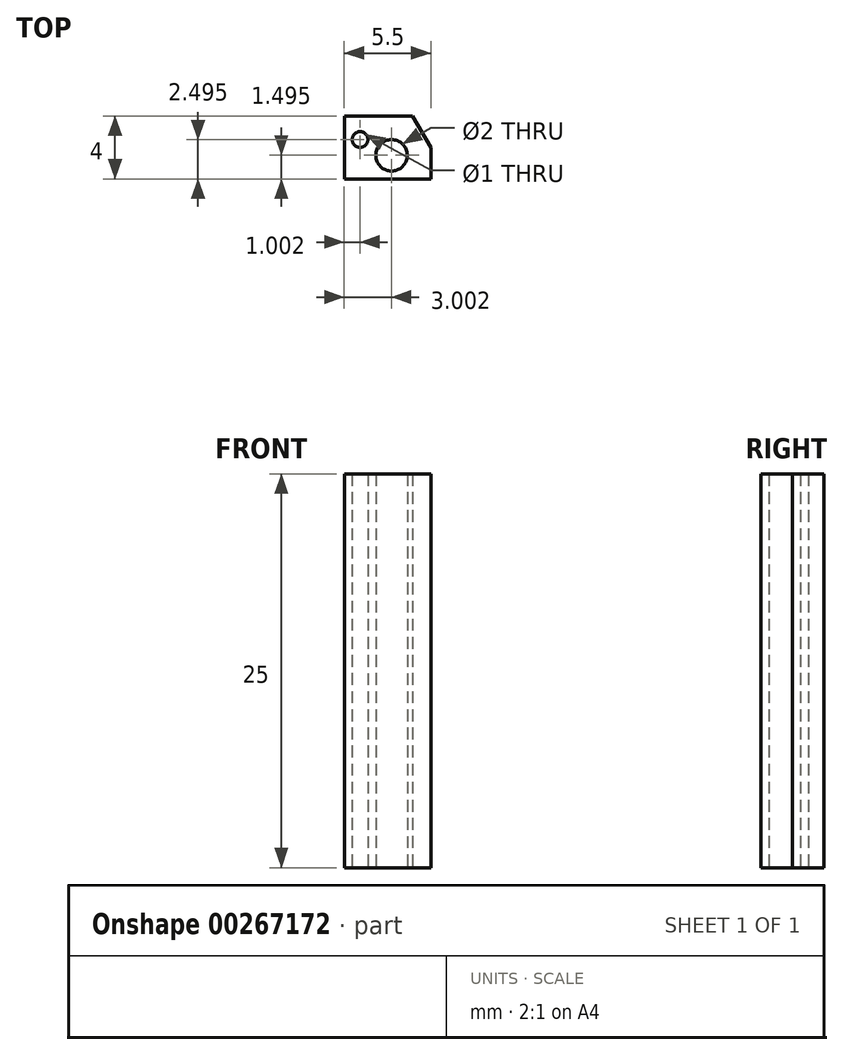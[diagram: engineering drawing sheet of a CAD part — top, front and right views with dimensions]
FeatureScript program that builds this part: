
annotation { "Feature Type Name" : "Feature", "Feature Type Description" : "" }
export const myFeature = defineFeature(function(context is Context, id is Id, definition is map)
    precondition{}
    {
        {
            var Q0;
            Q0=qCreatedBy(makeId("Top.planeOp"),FACE);
            var sketch = newSketch(context, id + "F0", { "sketchPlane" : qUnion([Q0])});
            skLineSegment(sketch, "E0", {"start": v(-60.06, -34.73) * mm, "end": v(-54.56, -34.73) * mm});
            skLineSegment(sketch, "E1", {"start": v(-54.56, -34.73) * mm, "end": v(-54.56, -32.73) * mm});
            skLineSegment(sketch, "E2", {"start": v(-54.56, -32.73) * mm, "end": v(-55.71, -30.73) * mm});
            skLineSegment(sketch, "E3", {"start": v(-55.71, -30.73) * mm, "end": v(-60.06, -30.73) * mm});
            skLineSegment(sketch, "E4", {"start": v(-60.06, -30.73) * mm, "end": v(-60.06, -34.73) * mm});
            skLineSegment(sketch, "E5", {"start": v(-54.56, -32.73) * mm, "end": v(-54.56, -30.68) * mm, "construction": true});
            skLineSegment(sketch, "E6", {"start": v(-60.06, -34.73) * mm, "end": v(-57.06, -34.73) * mm, "construction": true});
            skLineSegment(sketch, "E7", {"start": v(-57.06, -34.73) * mm, "end": v(-57.06, -32.96) * mm, "construction": true});
            skLineSegment(sketch, "E8", {"start": v(-54.56, -34.73) * mm, "end": v(-54.56, -33.23) * mm, "construction": true});
            skLineSegment(sketch, "E9", {"start": v(-54.56, -33.23) * mm, "end": v(-57.95, -33.23) * mm, "construction": true});
            skCircle(sketch, "E10", {"center": v(-57.06, -33.23) * mm, "radius": 0.5 * mm});
            skCircle(sketch, "E11", {"center": v(-57.06, -33.23) * mm, "radius": 1 * mm});
            skLineSegment(sketch, "E12", {"start": v(-60.06, -34.73) * mm, "end": v(-60.06, -32.23) * mm});
            skLineSegment(sketch, "E13", {"start": v(-60.06, -32.23) * mm, "end": v(-59.06, -32.23) * mm, "construction": true});
            skCircle(sketch, "E14", {"center": v(-59.06, -32.23) * mm, "radius": 0.5 * mm});
            skSolve(sketch);
        }
        {
            var Q0;
            Q0 = qSketchRegion(id + "F0", true);
            extrude(context, id + "F1", {"entities" : qUnion([Q0]), "depth" : 25 * mm});
        }
    });
